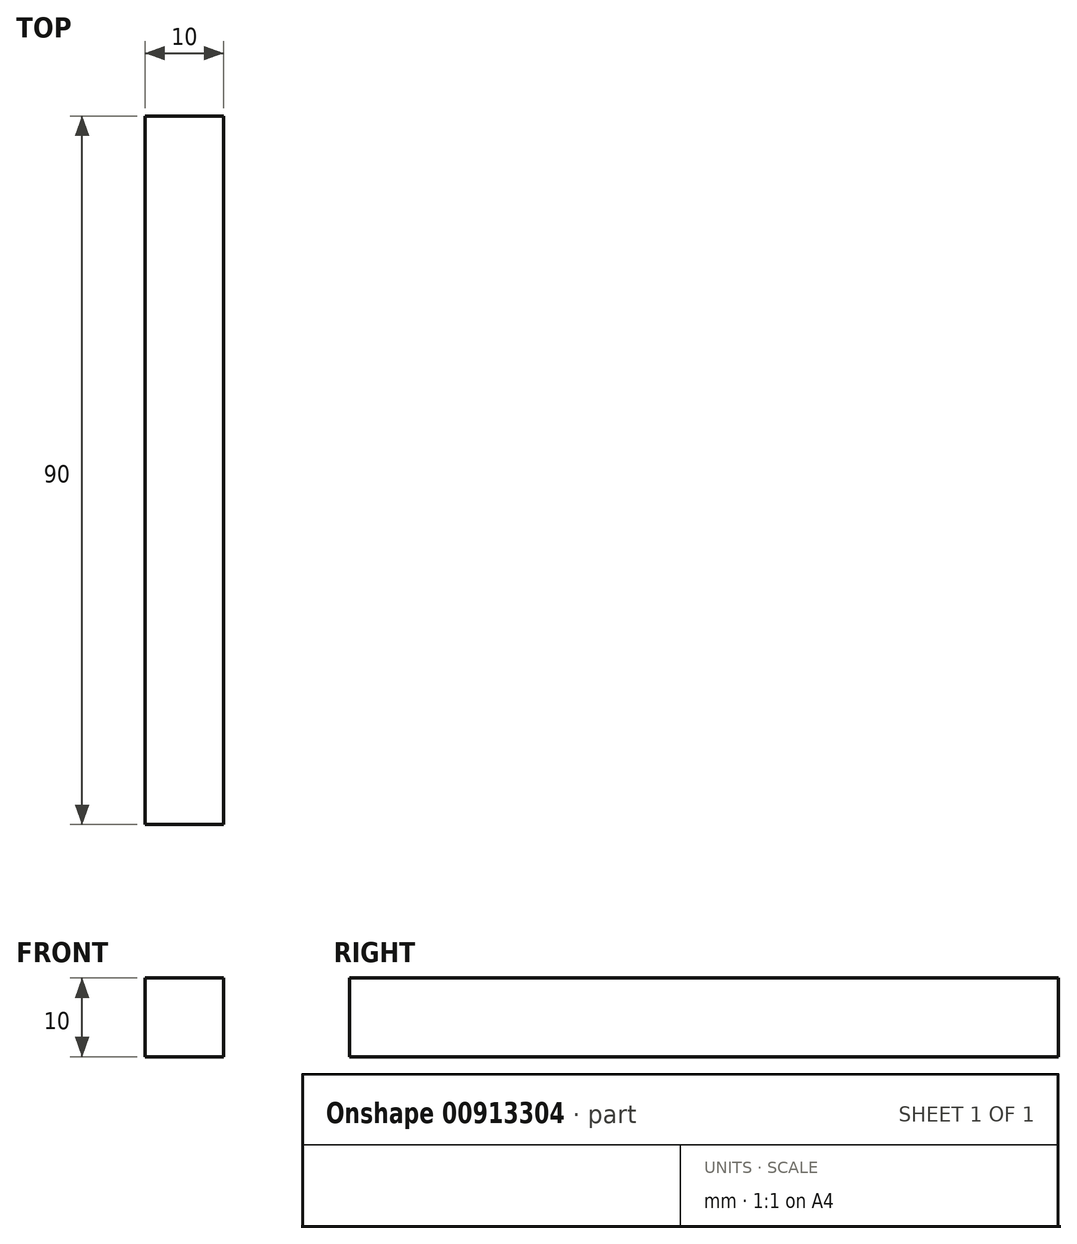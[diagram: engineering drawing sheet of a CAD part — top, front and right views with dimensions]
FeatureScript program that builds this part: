
annotation { "Feature Type Name" : "Feature", "Feature Type Description" : "" }
export const myFeature = defineFeature(function(context is Context, id is Id, definition is map)
    precondition{}
    {
        {
            var Q0;
            Q0=qCreatedBy(makeId("Top.planeOp"),FACE);
            var sketch = newSketch(context, id + "F0", { "sketchPlane" : qUnion([Q0])});
            skLineSegment(sketch, "E0.bottom", {"start": v(5, -45) * mm, "end": v(-5, -45) * mm});
            skLineSegment(sketch, "E0.top", {"start": v(5, 45) * mm, "end": v(-5, 45) * mm});
            skLineSegment(sketch, "E0.left", {"start": v(5, -45) * mm, "end": v(5, 45) * mm});
            skLineSegment(sketch, "E0.right", {"start": v(-5, -45) * mm, "end": v(-5, 45) * mm});
            skPoint(sketch, "E0.middle", {"position": v(0, 0) * mm});
            skSolve(sketch);
        }
        {
            var Q0;
            Q0=makeQuery(id+"F0.imprint","IMPRINT",FACE,{"disambiguationData":[TD([[makeQuery(id+"F0.imprint","IMPRINT",EDGE,{"derivedFrom":sQuery(id+"F0.wireOp",EDGE,"E0.bottom")}),-1.0]])]});
            extrude(context, id + "F1", {"entities" : qUnion([Q0]), "depth" : 10 * mm, "offsetDistance" : 25 * mm});
        }
        {
            var Q0;
            Q0=makeQuery(id+"F1.opExtrude","SWEPT_FACE",FACE,{"disambiguationData":[OSD([sQuery(id+"F0.wireOp",EDGE,"E0.right")])]});
            var sketch = newSketch(context, id + "F2", { "sketchPlane" : qUnion([Q0])});
            skFitSpline(sketch, "E1", {"points": [v(-45, 0) * mm, v(-22.85, 5.46) * mm, v(45, 7.67) * mm], "startDerivative": vector(115.23, 37.18) * mm, "endDerivative": vector(96.22, 6.16) * mm});
            skSolve(sketch);
        }
        {
            var Q0;
            {var subQ0=sQuery(id+"F2.wireOp",EDGE,"E1");Q0=makeQuery(id+"F2.imprint","IMPRINT",FACE,{"disambiguationData":[TD([[makeQuery(id+"F2.imprint","IMPRINT",EDGE,{"derivedFrom":subQ0}),-1.0]])]});}
            extrude(context, id + "F3", {"entities" : qUnion([Q0]), "oppositeDirection" : true, "depth" : 10 * mm, "offsetDistance" : 25 * mm});
        }
        {
            var Q0;
            Q0=makeQuery(id+"F1.opExtrude","SWEPT_FACE",FACE,{"disambiguationData":[OSD([sQuery(id+"F0.wireOp",EDGE,"E0.top")])]});
            var sketch = newSketch(context, id + "F4", { "sketchPlane" : qUnion([Q0])});
            skLineSegment(sketch, "E2", {"start": v(-5, 5) * mm, "end": v(5, 5) * mm});
            skLineSegment(sketch, "E3", {"start": v(0, 5) * mm, "end": v(0, 0) * mm});
            skSolve(sketch);
        }
        {
            var Q0;
            {var subQ4=sQuery(id+"F4.wireOp",EDGE,"E3");Q0=makeQuery(id+"F4.imprint","IMPRINT",FACE,{"disambiguationData":[TD([[makeQuery(id+"F4.imprint","IMPRINT",EDGE,{"derivedFrom":subQ4}),1.0]])]});}
            extrude(context, id + "F5", {"entities" : qUnion([Q0]), "operationType" : NewBodyOperationType.ADD, "oppositeDirection" : true, "depth" : 25 * mm, "offsetDistance" : 25 * mm});
        }
    });
